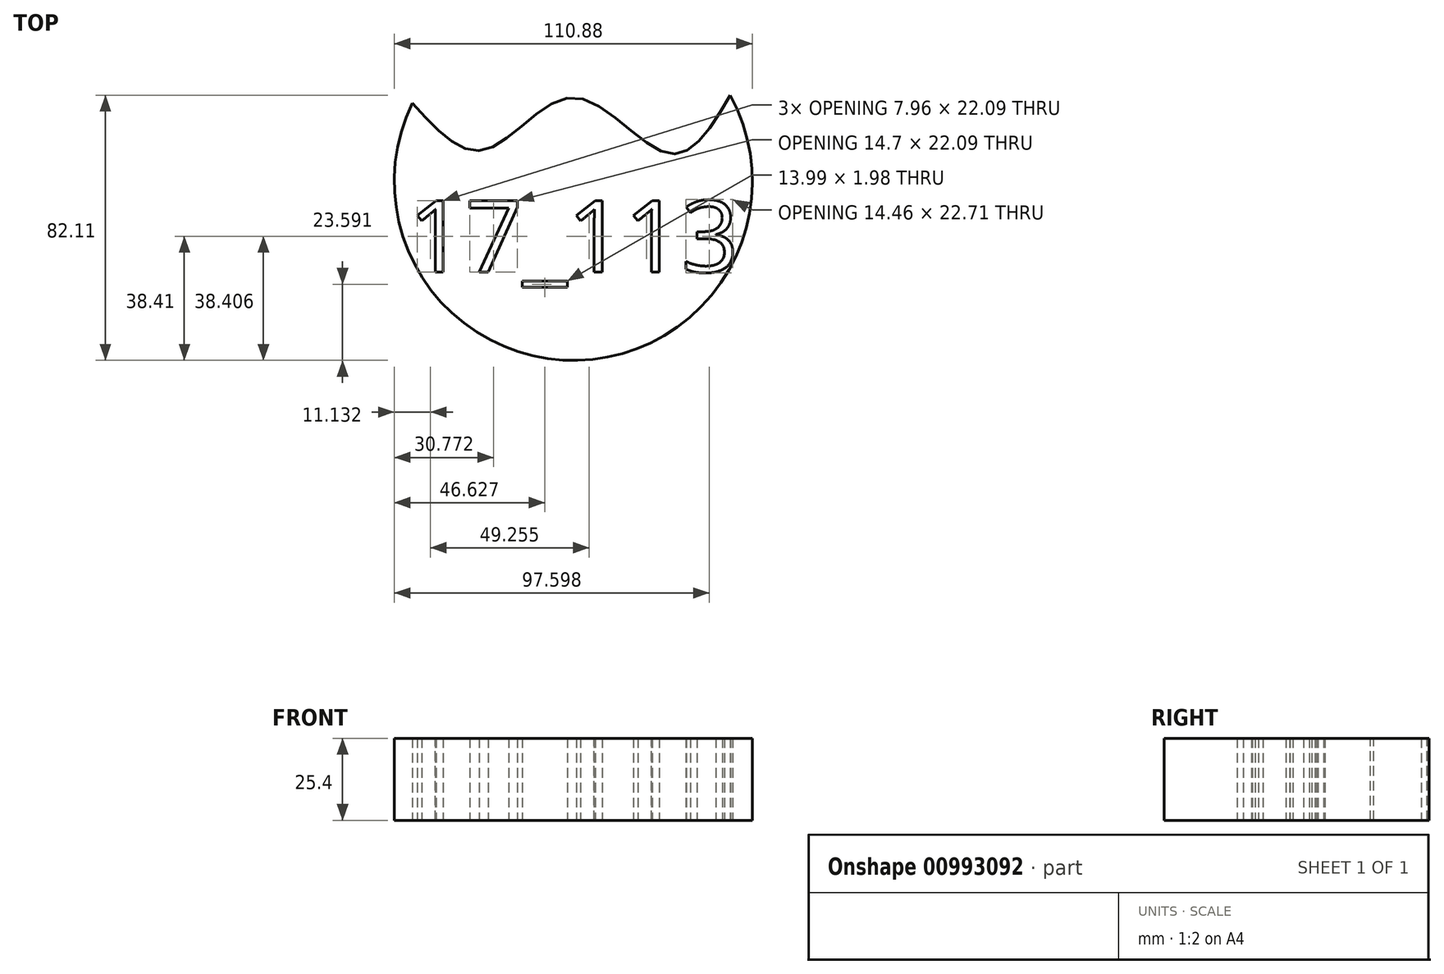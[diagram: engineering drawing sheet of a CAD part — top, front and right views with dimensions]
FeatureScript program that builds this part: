
annotation { "Feature Type Name" : "Feature", "Feature Type Description" : "" }
export const myFeature = defineFeature(function(context is Context, id is Id, definition is map)
    precondition{}
    {
        {
            var Q0;
            Q0=qCreatedBy(makeId("Top.planeOp"),FACE);
            var sketch = newSketch(context, id + "F0", { "sketchPlane" : qUnion([Q0])});
            skArc(sketch, "E0", {"start": v(-49.86, 24.23) * mm, "mid": v(1.37, -55.42) * mm, "end": v(48.6, 26.67) * mm});
            skFitSpline(sketch, "E1", {"points": [v(-49.86, 24.23) * mm, v(-27.32, 9.77) * mm, v(0, 25.95) * mm, v(29.76, 8.55) * mm, v(48.6, 26.67) * mm], "startDerivative": vector(92.92, -103.73) * mm, "endDerivative": vector(72.46, 123.68) * mm});
            skSolve(sketch);
        }
        {
            var Q0;
            Q0=makeQuery(id+"F0.imprint","IMPRINT",FACE,{"disambiguationData":[TD([[makeQuery(id+"F0.imprint","IMPRINT",EDGE,{"derivedFrom":sQuery(id+"F0.wireOp",EDGE,"E0")}),1.0]])]});
            extrude(context, id + "F1", {"entities" : qUnion([Q0]), "depth" : 25.4 * mm, "offsetDistance" : 25.4 * mm});
        }
        {
            var Q0;
            Q0=qCreatedBy(makeId("Top.planeOp"),FACE);
            var sketch = newSketch(context, id + "F2", { "sketchPlane" : qUnion([Q0])});
            skText(sketch, "E2", { "text": "17_113", "fontName": "OpenSans-Regular.ttf"});
            const initialGuessF2  = {"E2": [-0.03755, -0.03633, 1, 0, 0.01648]};
            skSetInitialGuess(sketch, initialGuessF2);
            skSolve(sketch);
        }
        {
            var Q0;
            Q0 = qSketchRegion(id + "F2", true);
            extrude(context, id + "F3", {"entities" : qUnion([Q0]), "operationType" : NewBodyOperationType.ADD, "depth" : 25.4 * mm, "offsetDistance" : 25.4 * mm});
        }
        {
            var Q0;
            Q0=qCreatedBy(makeId("Top.planeOp"),FACE);
            var sketch = newSketch(context, id + "F4", { "sketchPlane" : qUnion([Q0])});
            skText(sketch, "E3", { "text": "17_113", "fontName": "OpenSans-Regular.ttf"});
            const initialGuessF4  = {"E3": [-0.05113, -0.02808, 1, 0, 0.02228]};
            skSetInitialGuess(sketch, initialGuessF4);
            skSolve(sketch);
        }
        {
            var Q0;
            Q0 = qSketchRegion(id + "F4", true);
            extrude(context, id + "F5", {"entities" : qUnion([Q0]), "operationType" : NewBodyOperationType.REMOVE, "depth" : 25.4 * mm, "offsetDistance" : 25.4 * mm});
        }
    });
